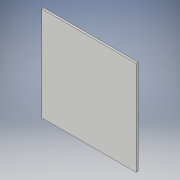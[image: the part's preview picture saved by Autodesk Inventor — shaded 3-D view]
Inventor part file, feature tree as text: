
AUTODESK INVENTOR PART (.ipt)
format: ipt  version: 2018 (Build 220112000, 112)  size: 88,576 bytes
history: native  units: in
note: dims shown in document units (in); Inventor stores cm internally (conversion verified against a paired STEP export)
features: extrude x1, sketch x1
ambient origin geometry x8: Origin, YZ Plane, XZ Plane, XY Plane, X Axis, Y Axis, Z Axis, Center Point
bodies: Solid1 (feature_tree)
feature tree (2):
  extrude  "Extrusion1"  Depth=17.3228in
  sketch  "Sketch1"  dims[d0=17.3228in d1=17.3228in d2=0.3937in d3=0.0in]
